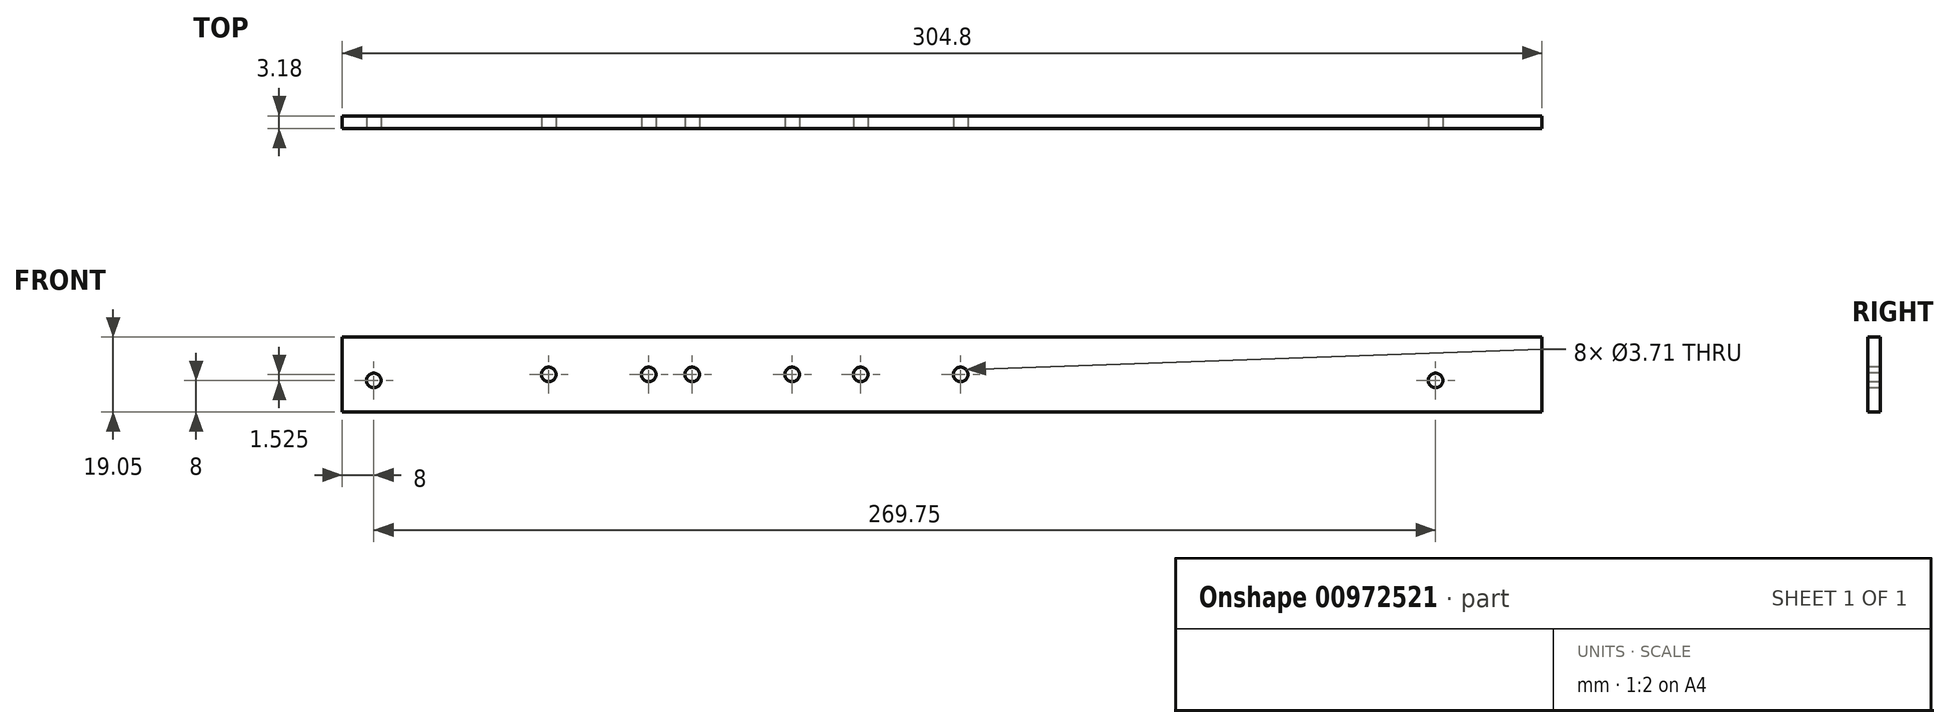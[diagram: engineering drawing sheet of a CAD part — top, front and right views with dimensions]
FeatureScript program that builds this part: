
annotation { "Feature Type Name" : "Feature", "Feature Type Description" : "" }
export const myFeature = defineFeature(function(context is Context, id is Id, definition is map)
    precondition{}
    {
        {
            var Q0;
            Q0=qCreatedBy(makeId("Front.planeOp"),FACE);
            var sketch = newSketch(context, id + "F0", { "sketchPlane" : qUnion([Q0])});
            skLineSegment(sketch, "E0.bottom", {"start": v(0, 0) * mm, "end": v(-304.8, 0) * mm});
            skLineSegment(sketch, "E0.top", {"start": v(0, 19.05) * mm, "end": v(-304.8, 19.05) * mm});
            skLineSegment(sketch, "E0.left", {"start": v(0, 0) * mm, "end": v(0, 19.05) * mm});
            skLineSegment(sketch, "E0.right", {"start": v(-304.8, 0) * mm, "end": v(-304.8, 19.05) * mm});
            skSolve(sketch);
        }
        {
            var Q0;
            Q0=makeQuery(id+"F0.imprint","IMPRINT",FACE,{"disambiguationData":[TD([[makeQuery(id+"F0.imprint","IMPRINT",EDGE,{"derivedFrom":sQuery(id+"F0.wireOp",EDGE,"E0.bottom")}),-1.0]])]});
            extrude(context, id + "F1", {"entities" : qUnion([Q0]), "depth" : 3.17 * mm, "offsetDistance" : 25.4 * mm});
        }
        {
            var Q0;
            Q0=makeQuery(id+"F1.opExtrude","CAP_FACE",FACE,{"disambiguationData":[OSD([sQuery(id+"F0.wireOp",EDGE,"E0.bottom"),sQuery(id+"F0.wireOp",EDGE,"E0.top"),sQuery(id+"F0.wireOp",EDGE,"E0.left"),sQuery(id+"F0.wireOp",EDGE,"E0.right")])],"isStart":false});
            var sketch = newSketch(context, id + "F2", { "sketchPlane" : qUnion([Q0])});
            skCircle(sketch, "E1", {"center": v(-296.8, 8) * mm, "radius": 1.86 * mm});
            skCircle(sketch, "E2", {"center": v(-252.35, 9.52) * mm, "radius": 1.86 * mm});
            skPoint(sketch, "E2.centerSnap0", {"position": v(-304.8, 9.52) * mm});
            skCircle(sketch, "E3", {"center": v(-226.95, 9.52) * mm, "radius": 1.86 * mm});
            skCircle(sketch, "E4", {"center": v(-215.9, 9.52) * mm, "radius": 1.85 * mm});
            skCircle(sketch, "E5", {"center": v(-190.5, 9.52) * mm, "radius": 1.86 * mm});
            skCircle(sketch, "E6", {"center": v(-173.1, 9.52) * mm, "radius": 1.85 * mm});
            skCircle(sketch, "E7", {"center": v(-147.7, 9.52) * mm, "radius": 1.86 * mm});
            skCircle(sketch, "E8", {"center": v(-27.05, 8) * mm, "radius": 1.86 * mm});
            skSolve(sketch);
        }
        {
            var Q0;
            Q0=makeQuery(id+"F2.imprint","IMPRINT",FACE,{"disambiguationData":[TD([[makeQuery(id+"F2.imprint","IMPRINT",EDGE,{"derivedFrom":sQuery(id+"F2.wireOp",EDGE,"E1")}),1.0]])]});
            var Q1;
            Q1=makeQuery(id+"F2.imprint","IMPRINT",FACE,{"disambiguationData":[TD([[makeQuery(id+"F2.imprint","IMPRINT",EDGE,{"derivedFrom":sQuery(id+"F2.wireOp",EDGE,"E4")}),1.0]])]});
            var Q2;
            Q2=makeQuery(id+"F2.imprint","IMPRINT",FACE,{"disambiguationData":[TD([[makeQuery(id+"F2.imprint","IMPRINT",EDGE,{"derivedFrom":sQuery(id+"F2.wireOp",EDGE,"E2")}),1.0]])]});
            var Q3;
            Q3=makeQuery(id+"F2.imprint","IMPRINT",FACE,{"disambiguationData":[TD([[makeQuery(id+"F2.imprint","IMPRINT",EDGE,{"derivedFrom":sQuery(id+"F2.wireOp",EDGE,"E3")}),1.0]])]});
            var Q4;
            Q4=makeQuery(id+"F2.imprint","IMPRINT",FACE,{"disambiguationData":[TD([[makeQuery(id+"F2.imprint","IMPRINT",EDGE,{"derivedFrom":sQuery(id+"F2.wireOp",EDGE,"E5")}),1.0]])]});
            var Q5;
            Q5=makeQuery(id+"F2.imprint","IMPRINT",FACE,{"disambiguationData":[TD([[makeQuery(id+"F2.imprint","IMPRINT",EDGE,{"derivedFrom":sQuery(id+"F2.wireOp",EDGE,"E6")}),1.0]])]});
            var Q6;
            Q6=makeQuery(id+"F2.imprint","IMPRINT",FACE,{"disambiguationData":[TD([[makeQuery(id+"F2.imprint","IMPRINT",EDGE,{"derivedFrom":sQuery(id+"F2.wireOp",EDGE,"E7")}),1.0]])]});
            var Q7;
            Q7=makeQuery(id+"F2.imprint","IMPRINT",FACE,{"disambiguationData":[TD([[makeQuery(id+"F2.imprint","IMPRINT",EDGE,{"derivedFrom":sQuery(id+"F2.wireOp",EDGE,"E8")}),1.0]])]});
            extrude(context, id + "F3", {"entities" : qUnion([Q0, Q1, Q2, Q3, Q4, Q5, Q6, Q7]), "operationType" : NewBodyOperationType.REMOVE, "oppositeDirection" : true, "depth" : 3.17 * mm, "offsetDistance" : 25.4 * mm});
        }
    });
